# Revit family: AV1020001_Grifería para lavamanos 4 pulgadas Aluvia triceta
name_source: partatom
category: Plumbing Fixtures
units: mm (PartAtom-declared; Revit-internal decimal feet)

## family parameters
Cut with Voids When Loaded = No
Host = Face
OmniClass Number = 23.31.11.00
OmniClass Title = Faucets
Part Type = Normal
Room Calculation Point = No
Round Connector Dimension = Use Diameter
Shared = No

## types (1)
- AV1020001_Grifería para lavamanos 4 pulgadas Aluvia triceta
    Alto = 104 mm
    Ancho = 218 mm
    Capacidad de flujo = 60 psi : 5,7 L/min.
    Default Elevation = 1219 mm
    Description = Aluvia integra líneas y formas como las de una erosión aluvial, su forma robusta está inspirada en el agua esculpiendo las rocas a través de los años dando paso a superficies más suaves, amigables y limpias evitando que haya acumulación de impurezas. El conjunto de manijas es el resultado de su diseño ergonómico, brindando un agarre cómodo sin importar el agua y el jabón • Grifería ultra ahorro, consumo de 5,7 litros por minuto.
• Cierre fácil giro práctico de tan sólo 90º.
• Acabado superior, mayor espesor en el cromado que lo hace más brillante y
resistente a la corrosión.
• Mayor ángulo de salida permite mayor alcance y más comodidad en el
momento del uso.
• Fácil limpieza: Diseño que evita la acumulación de impurezas.
    Garantía = 30 Años
    Garantía Acabado = 2 Años
    Longitud = 156 mm
    MATERIAL = Corona_Cromado
    Manufacturer = Corona
    Model = Grifería lavamanos 4 pulgadas palanca Aluvia
    Peso neto = 330 gr. - 0,72 lb.
    Presión máxima recomendada = 125 psi (862 Kpa).
    Presión mínima recomendada = 20 psi (138 Kpa)
    Temperatura de uso = 5ºC a 71ºC.
    URL = https://corona.co
    Vida útil o desgaste (unidad) = 500.000 ciclos.

## geometry (parser evidence)
native form markers: Sweep x5
no freeform markers — native parametric forms only
